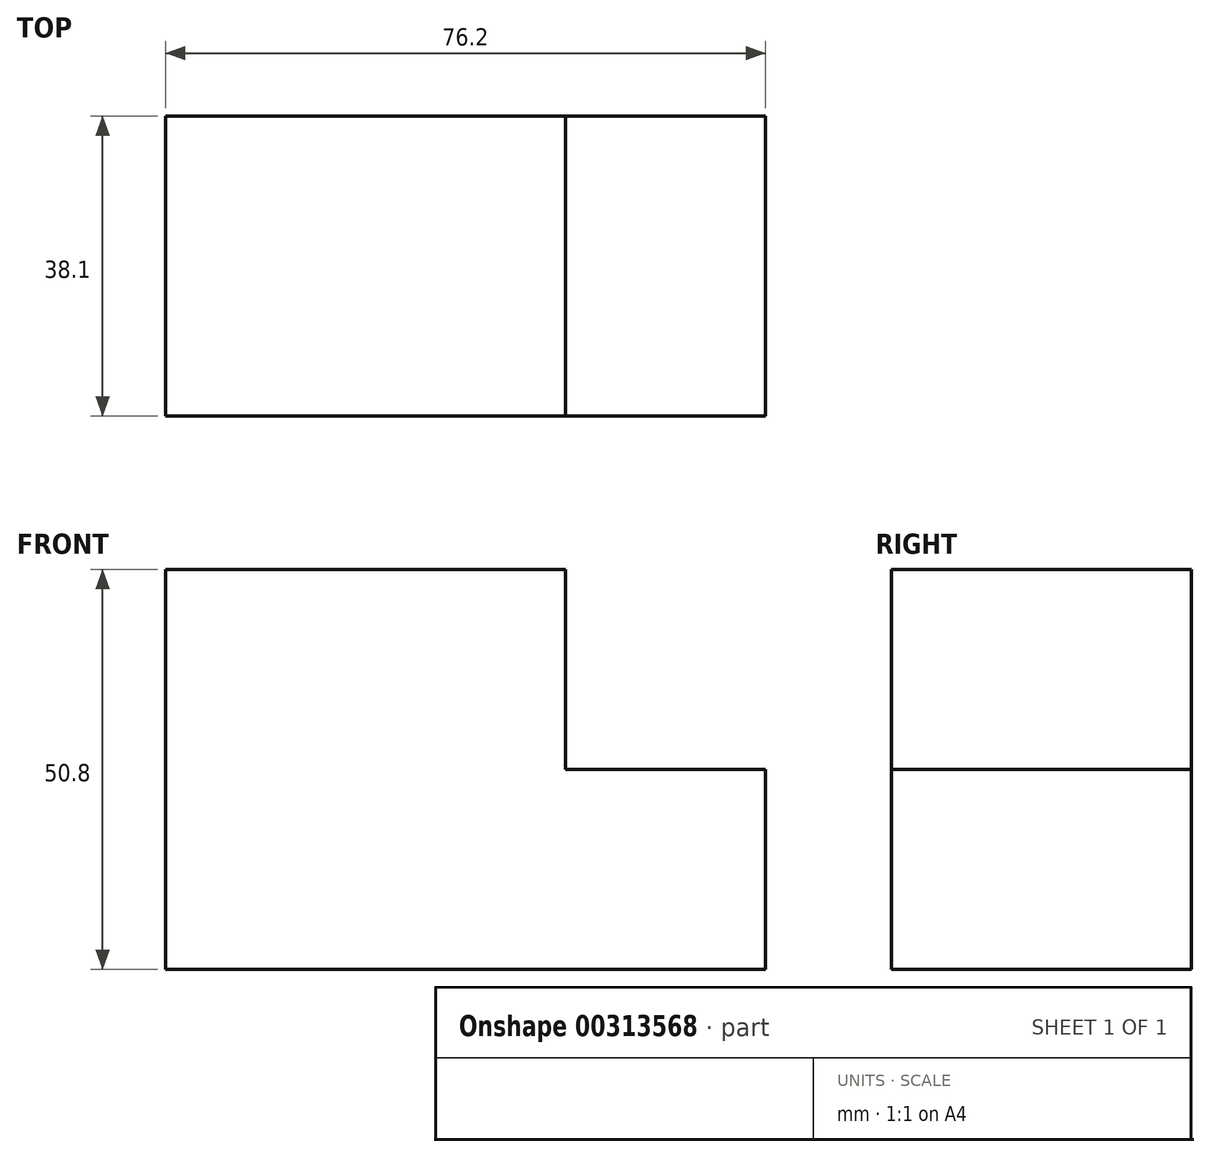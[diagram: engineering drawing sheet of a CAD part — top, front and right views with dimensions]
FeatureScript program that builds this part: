
annotation { "Feature Type Name" : "Feature", "Feature Type Description" : "" }
export const myFeature = defineFeature(function(context is Context, id is Id, definition is map)
    precondition{}
    {
        {
            var Q0;
            Q0=qCreatedBy(makeId("Front.planeOp"),FACE);
            var sketch = newSketch(context, id + "F0", { "sketchPlane" : qUnion([Q0])});
            skLineSegment(sketch, "E0", {"start": v(-38.1, 25.4) * mm, "end": v(12.7, 25.4) * mm});
            skLineSegment(sketch, "E1", {"start": v(12.7, 25.4) * mm, "end": v(12.7, 0) * mm});
            skLineSegment(sketch, "E2", {"start": v(12.7, 0) * mm, "end": v(38.1, 0) * mm});
            skLineSegment(sketch, "E3", {"start": v(38.1, 0) * mm, "end": v(38.1, -25.4) * mm});
            skLineSegment(sketch, "E4", {"start": v(38.1, -25.4) * mm, "end": v(-38.1, -25.4) * mm});
            skLineSegment(sketch, "E5", {"start": v(-38.1, -25.4) * mm, "end": v(-38.1, 25.4) * mm});
            skSolve(sketch);
        }
        {
            var Q0;
            Q0=makeQuery(id+"F0.imprint","IMPRINT",FACE,{"disambiguationData":[TD([[makeQuery(id+"F0.imprint","IMPRINT",EDGE,{"derivedFrom":sQuery(id+"F0.wireOp",EDGE,"E0")}),-1.0]])]});
            extrude(context, id + "F1", {"entities" : qUnion([Q0]), "depth" : 38.1 * mm});
        }
    });
